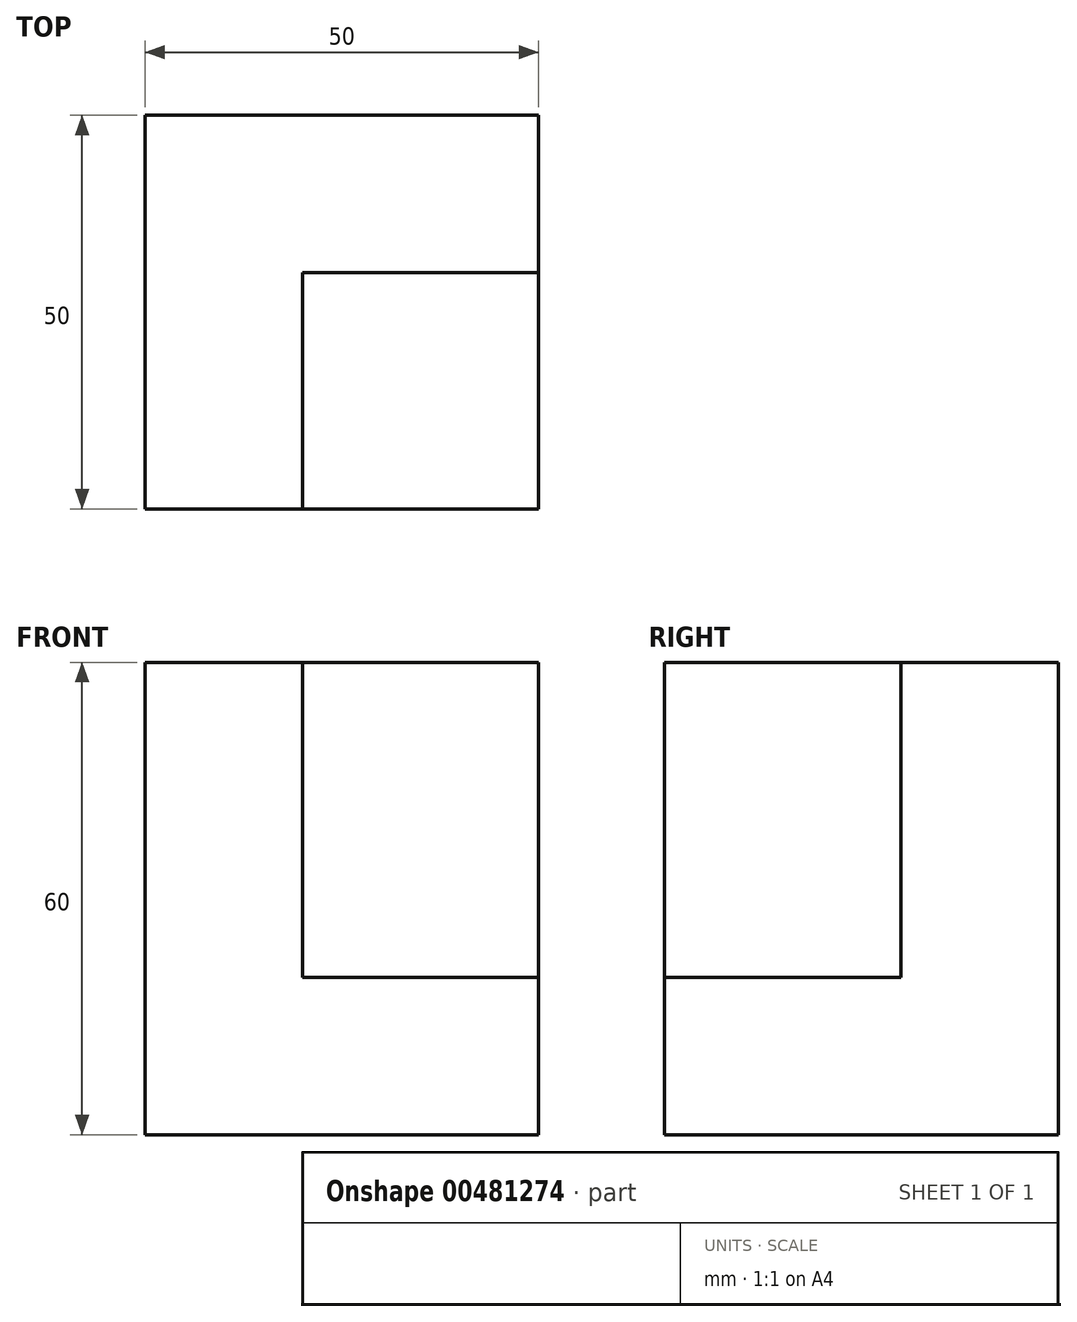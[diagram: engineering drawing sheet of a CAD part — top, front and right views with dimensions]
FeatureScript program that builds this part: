
annotation { "Feature Type Name" : "Feature", "Feature Type Description" : "" }
export const myFeature = defineFeature(function(context is Context, id is Id, definition is map)
    precondition{}
    {
        {
            var Q0;
            Q0=qCreatedBy(makeId("Front.planeOp"),FACE);
            var sketch = newSketch(context, id + "F0", { "sketchPlane" : qUnion([Q0])});
            skLineSegment(sketch, "E0", {"start": v(0, 0) * mm, "end": v(0, 60) * mm});
            skLineSegment(sketch, "E1", {"start": v(0, 60) * mm, "end": v(20, 60) * mm});
            skLineSegment(sketch, "E2", {"start": v(20, 60) * mm, "end": v(20, 20) * mm});
            skLineSegment(sketch, "E3", {"start": v(20, 20) * mm, "end": v(50, 20) * mm});
            skLineSegment(sketch, "E4", {"start": v(50, 20) * mm, "end": v(50, 0) * mm});
            skLineSegment(sketch, "E5", {"start": v(50, 0) * mm, "end": v(0, 0) * mm});
            skSolve(sketch);
        }
        {
            var Q0;
            Q0=makeQuery(id+"F0.imprint","IMPRINT",FACE,{"disambiguationData":[TD([[makeQuery(id+"F0.imprint","IMPRINT",EDGE,{"derivedFrom":sQuery(id+"F0.wireOp",EDGE,"E0")}),-1.0]])]});
            extrude(context, id + "F1", {"entities" : qUnion([Q0]), "depth" : 50 * mm});
        }
        {
            var Q0;
            Q0=makeQuery(id+"F1.opExtrude","CAP_FACE",FACE,{"disambiguationData":[OSD([sQuery(id+"F0.wireOp",EDGE,"E0"),sQuery(id+"F0.wireOp",EDGE,"E1"),sQuery(id+"F0.wireOp",EDGE,"E2"),sQuery(id+"F0.wireOp",EDGE,"E3"),sQuery(id+"F0.wireOp",EDGE,"E4"),sQuery(id+"F0.wireOp",EDGE,"E5")])],"isStart":true});
            var sketch = newSketch(context, id + "F2", { "sketchPlane" : qUnion([Q0])});
            skLineSegment(sketch, "E6.bottom", {"start": v(-20, 60) * mm, "end": v(-50, 60) * mm});
            skLineSegment(sketch, "E6.top", {"start": v(-20, 20) * mm, "end": v(-50, 20) * mm});
            skLineSegment(sketch, "E6.left", {"start": v(-20, 60) * mm, "end": v(-20, 20) * mm});
            skLineSegment(sketch, "E6.right", {"start": v(-50, 60) * mm, "end": v(-50, 20) * mm});
            skSolve(sketch);
        }
        {
            var Q0;
            Q0 = qSketchRegion(id + "F2", true);
            extrude(context, id + "F3", {"entities" : qUnion([Q0]), "operationType" : NewBodyOperationType.ADD, "oppositeDirection" : true, "depth" : 20 * mm});
        }
    });
